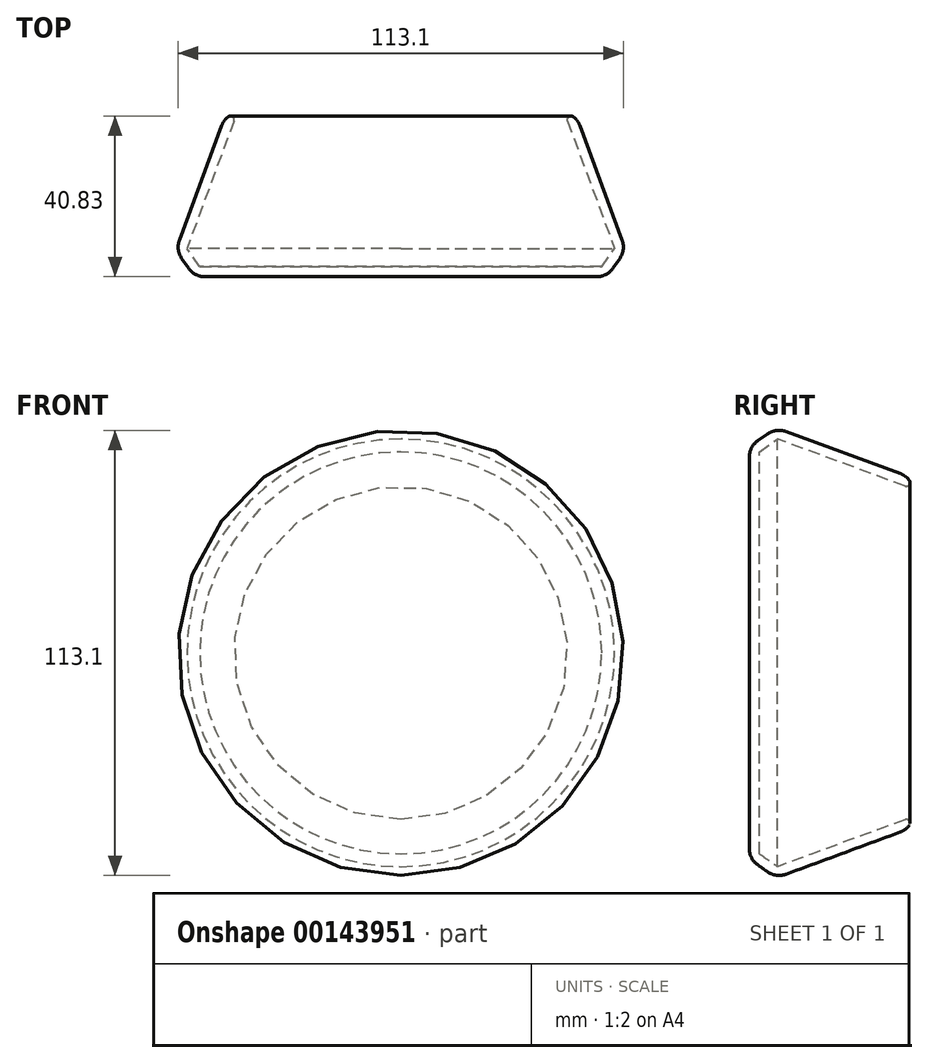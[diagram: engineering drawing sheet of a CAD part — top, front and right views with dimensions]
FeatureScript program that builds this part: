
annotation { "Feature Type Name" : "Feature", "Feature Type Description" : "" }
export const myFeature = defineFeature(function(context is Context, id is Id, definition is map)
    precondition{}
    {
        {
            var Q0;
            Q0=qCreatedBy(makeId("Front.planeOp"),FACE);
            cPlane(context, id + "F0", {"entities" : qUnion([Q0]), "cplaneType" : CPlaneType.OFFSET, "offset" : 50.8 * mm, "oppositeDirection" : true, "width" : 152.4 * mm, "height" : 152.4 * mm});
        }
        {
            var Q0;
            Q0=qCreatedBy(makeId("Front.planeOp"),FACE);
            var sketch = newSketch(context, id + "F1", { "sketchPlane" : qUnion([Q0])});
            skCircle(sketch, "E0", {"center": v(0, 0) * mm, "radius": 59.68 * mm});
            skSolve(sketch);
        }
        {
            var Q0;
            Q0=qCreatedBy(id+"F0.planeOp",FACE);
            var sketch = newSketch(context, id + "F2", { "sketchPlane" : qUnion([Q0])});
            skCircle(sketch, "E1", {"center": v(0, 0) * mm, "radius": 40.94 * mm});
            skSolve(sketch);
        }
        {
            var Q0;
            Q0=makeQuery(id+"F2.imprint","IMPRINT",FACE,{"disambiguationData":[TD([[makeQuery(id+"F2.imprint","IMPRINT",EDGE,{"derivedFrom":sQuery(id+"F2.wireOp",EDGE,"E1")}),1.0]])]});
            var Q1;
            Q1=makeQuery(id+"F1.imprint","IMPRINT",FACE,{"disambiguationData":[TD([[makeQuery(id+"F1.imprint","IMPRINT",EDGE,{"derivedFrom":sQuery(id+"F1.wireOp",EDGE,"E0")}),1.0]])]});
            var Q2;
            Q2=sQuery(id+"F2.wireOp",EDGE,"E1");
            var Q3;
            Q3=sQuery(id+"F1.wireOp",EDGE,"E0");
            loft(context, id + "F3", {"sheetProfilesArray" : [{ "sheetProfileEntities" : qUnion([Q0]) }, { "sheetProfileEntities" : qUnion([Q1]) }], "wireProfilesArray" : [{ "wireProfileEntities" : qUnion([Q2]) }, { "wireProfileEntities" : qUnion([Q3]) }]});
        }
        {
            var Q0;
            Q0=makeQuery(id+"F3.opLoft","MID_CAP_EDGE",EDGE,{"disambiguationData":[OSD([sQuery(id+"F2.wireOp",EDGE,"E1")])],"capPos":0.0});
            fillet(context, id + "F4", {"entities" : qUnion([Q0]), "radius" : 12.7 * mm, "tangentPropagation" : true, "allowEdgeOverflow" : false});
        }
        {
            var Q0;
            Q0=makeQuery(id+"F3.opLoft","MID_CAP_EDGE",EDGE,{"disambiguationData":[OSD([sQuery(id+"F1.wireOp",EDGE,"E0"),sQuery(id+"F2.wireOp",EDGE,"E1")])],"capPos":1.0});
            chamfer(context, id + "F5", {"entities" : qUnion([Q0]), "width" : 5.08 * mm, "tangentPropagation" : true});
        }
        {
            var Q0;
            Q0=makeQuery(id+"F3.opLoft","CAP_FACE",FACE,{"disambiguationData":[OSD([makeQuery(id+"F2.imprint","IMPRINT",FACE,{"disambiguationData":[TD([[makeQuery(id+"F2.imprint","IMPRINT",EDGE,{"derivedFrom":sQuery(id+"F2.wireOp",EDGE,"E1")}),1.0]])]})])],"isStart":true});
            var Q1;
            Q1=makeQuery(id+"F4.opFillet","BLEND_FACE",FACE,{"disambiguationData":[OSD([sQuery(id+"F2.wireOp",EDGE,"E1")])]});
            shell(context, id + "F6", {"entities" : qUnion([Q0, Q1]), "thickness" : 2.54 * mm});
        }
        {
            var Q0;
            {var subQ0=sQuery(id+"F2.wireOp",EDGE,"E1");var subQ1=sQuery(id+"F1.wireOp",EDGE,"E0");Q0=makeQuery(id+"F6.opShell","OFFSET_EDGE",EDGE,{"disambiguationData":[OSD([subQ1,subQ0]),TDD([makeQuery(id+"F4.opFillet","BLEND_EDGE",EDGE,{"blendedFrom":[makeQuery(id+"F3.opLoft","MID_CAP_EDGE",EDGE,{"disambiguationData":[OSD([subQ0])],"capPos":0.0}),makeQuery(id+"F3.opLoft","SWEPT_FACE",FACE,{"disambiguationData":[OSD([subQ1,subQ0])]})],"blendedInto":[makeQuery(id+"F3.opLoft","SWEPT_FACE",FACE,{"disambiguationData":[OSD([subQ1,subQ0])]})]})]),OD(0.0)]});}
            fillet(context, id + "F7", {"entities" : qUnion([Q0]), "radius" : 5.08 * mm, "tangentPropagation" : true, "allowEdgeOverflow" : false});
        }
        {
            var Q0;
            {var subQ0=sQuery(id+"F2.wireOp",EDGE,"E1");var subQ1=sQuery(id+"F1.wireOp",EDGE,"E0");Q0=makeQuery(id+"F5.opChamfer","BLEND_EDGE",EDGE,{"blendedFrom":[makeQuery(id+"F3.opLoft","MID_CAP_EDGE",EDGE,{"disambiguationData":[OSD([subQ1,subQ0])],"capPos":1.0}),makeQuery(id+"F3.opLoft","SWEPT_FACE",FACE,{"disambiguationData":[OSD([subQ1,subQ0])]})],"blendedInto":[makeQuery(id+"F3.opLoft","SWEPT_FACE",FACE,{"disambiguationData":[OSD([subQ1,subQ0])]})]});}
            fillet(context, id + "F8", {"entities" : qUnion([Q0]), "radius" : 5.08 * mm, "tangentPropagation" : true, "allowEdgeOverflow" : false});
        }
        {
            var Q0;
            {var subQ0=sQuery(id+"F1.wireOp",EDGE,"E0");Q0=makeQuery(id+"F5.opChamfer","BLEND_EDGE",EDGE,{"blendedFrom":[makeQuery(id+"F3.opLoft","MID_CAP_EDGE",EDGE,{"disambiguationData":[OSD([subQ0,sQuery(id+"F2.wireOp",EDGE,"E1")])],"capPos":1.0}),makeQuery(id+"F3.opLoft","CAP_FACE",FACE,{"disambiguationData":[OSD([makeQuery(id+"F1.imprint","IMPRINT",FACE,{"disambiguationData":[TD([[makeQuery(id+"F1.imprint","IMPRINT",EDGE,{"derivedFrom":subQ0}),1.0]])]})])],"isStart":true})],"blendedInto":[makeQuery(id+"F3.opLoft","CAP_FACE",FACE,{"disambiguationData":[OSD([makeQuery(id+"F1.imprint","IMPRINT",FACE,{"disambiguationData":[TD([[makeQuery(id+"F1.imprint","IMPRINT",EDGE,{"derivedFrom":subQ0}),1.0]])]})])],"isStart":true})]});}
            fillet(context, id + "F9", {"entities" : qUnion([Q0]), "radius" : 5.08 * mm, "tangentPropagation" : true, "allowEdgeOverflow" : false});
        }
        {
            var Q0;
            {var subQ0=sQuery(id+"F2.wireOp",EDGE,"E1");var subQ1=sQuery(id+"F1.wireOp",EDGE,"E0");var subQ2=makeQuery(id+"F3.opLoft","SWEPT_FACE",FACE,{"disambiguationData":[OSD([subQ1,subQ0])]});Q0=makeQuery(id+"F7.opFillet","BLEND_EDGE",EDGE,{"blendedFrom":[makeQuery(id+"F6.opShell","OFFSET_EDGE",EDGE,{"disambiguationData":[OSD([subQ1,subQ0]),TDD([makeQuery(id+"F4.opFillet","BLEND_EDGE",EDGE,{"blendedFrom":[makeQuery(id+"F3.opLoft","MID_CAP_EDGE",EDGE,{"disambiguationData":[OSD([subQ0])],"capPos":0.0}),subQ2],"blendedInto":[subQ2]})]),OD(0.0)]}),makeQuery(id+"F6.opShell","OFFSET_FACE",FACE,{"disambiguationData":[OSD([subQ1,subQ0]),TDD([subQ2])]})],"blendedInto":[makeQuery(id+"F6.opShell","OFFSET_FACE",FACE,{"disambiguationData":[OSD([subQ1,subQ0]),TDD([subQ2])]})]});}
            fillet(context, id + "F10", {"entities" : qUnion([Q0]), "radius" : 0.96 * mm, "tangentPropagation" : true, "allowEdgeOverflow" : false});
        }
    });
